# Revit family: 47380 Ifö Sense Furniture packs - SDSSMP 60 Compact
name_source: partatom
category: Generic Models
revit_build: Autodesk Revit 2015 (Build: 20140606_1530(x64)
units: mm (PartAtom-declared; Revit-internal decimal feet)

## types (1)
- 47380 Ifö Sense Furniture packs with doors SDSSMP 60 Compact, white
    BIMObjectName = 47380 Ifö Sense Furniture packs - SDSSMP 60 Compact
    Brand = Ifö
    CabinetMaterial = MDF Chipboard
    Category = WashHandBasin
    Color = White
    ConnectorIn_HDistance = 120.00 mm
    ConnectorIn_VDistance = 0.00 mm
    Depth = 375.00 mm
    Description = Ifö Sense furniture pack with doors Compact 60 cm
    DrainSize = 0.00 mm
    Features = feature1, feature2, feature55
    Fittings = Metal-Steel
    Handle = Metal-Steel
    Height = 535.00 mm
    Manufacturer = Geberit
    Material = MDF Chipboard, Porcelain
    Mixernotincluded(option) = Yes
    Model = Ifö Sense Furniture packs with doors SDSSMP 60 Compact, white
    ModelNumber = 47380
    ModelReference = Sense
    MountingHeight(offset) = 850.00 mm
    Name = Ifö Sense furniture pack with doors Compact 60 cm
    NominalDepth = 375.00 mm
    NominalHeight = 535.00 mm
    NominalWidth = 615.00 mm
    OutputFileName = 47380 Ifö Sense Furniture packs with doors SDSSMP 60 Compact, white
    Panel = White
    ReturnPipeDiameter = 32.00 mm
    Serie = Sense
    Shape = Square
    SinkVerticalOffset = 844.63 mm
    Size = 615x535x375
    SupplyPipeDiameter = 10.00 mm
    Type = Building element
    URL.dk = http://www.ifo.dk
    URL.no = http://www.ifosanitar.no
    URL.se = http://www.ifo.se
    Width = 615.00 mm
    ifcExportAs = ifcSanitaryTerminalType
    ifcExportType = WASHHANDBASIN

## geometry (parser evidence)
native form markers: Blend x2, Sweep x2
no freeform markers — native parametric forms only
